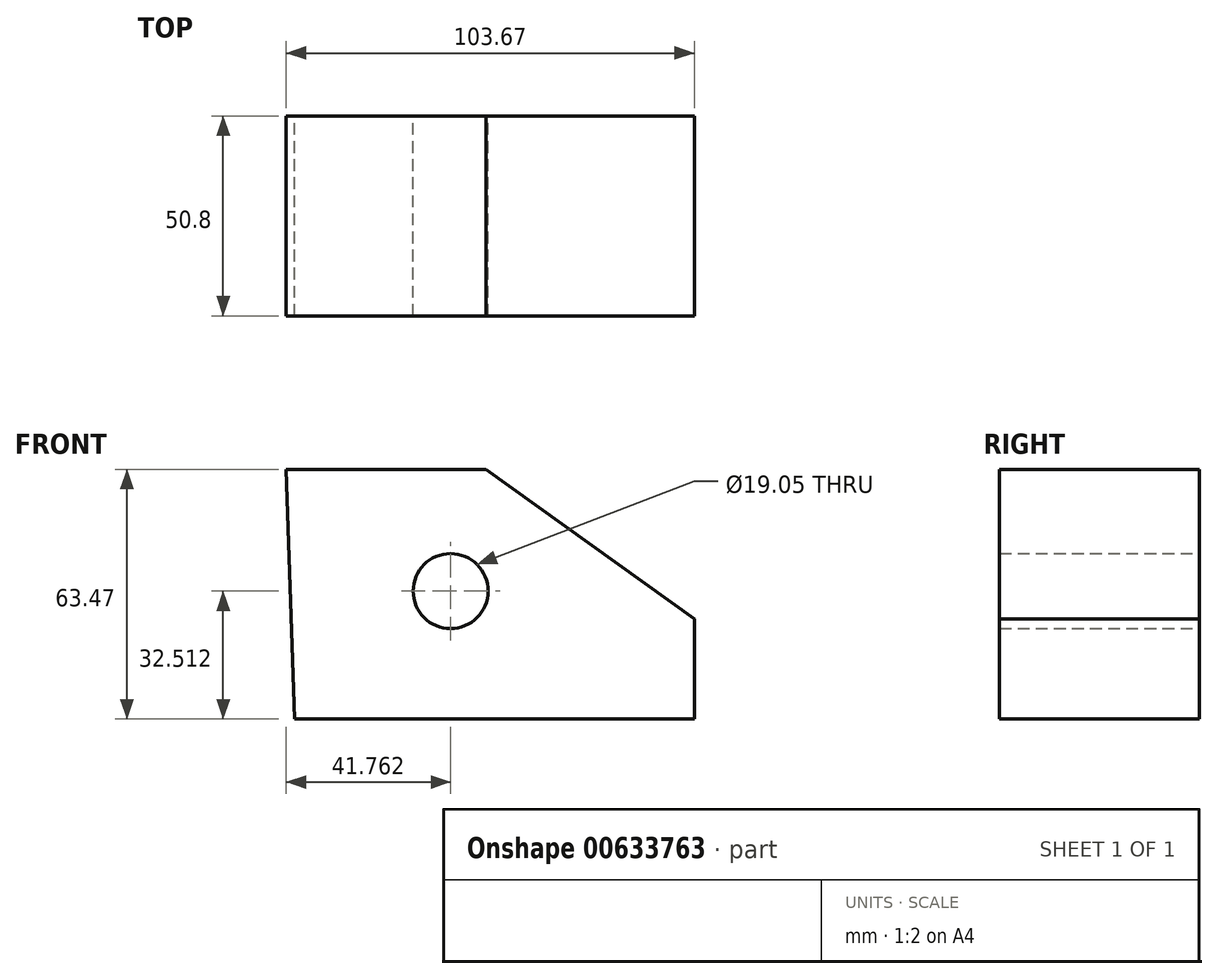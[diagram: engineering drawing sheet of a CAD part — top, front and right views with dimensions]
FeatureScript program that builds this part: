
annotation { "Feature Type Name" : "Feature", "Feature Type Description" : "" }
export const myFeature = defineFeature(function(context is Context, id is Id, definition is map)
    precondition{}
    {
        {
            var Q0;
            Q0=qCreatedBy(makeId("Front.planeOp"),FACE);
            var sketch = newSketch(context, id + "F0", { "sketchPlane" : qUnion([Q0])});
            skLineSegment(sketch, "E0", {"start": v(-48.04, 48.04) * mm, "end": v(2.76, 48.04) * mm});
            skLineSegment(sketch, "E1", {"start": v(2.76, 48.04) * mm, "end": v(55.63, 9.97) * mm});
            skLineSegment(sketch, "E2", {"start": v(55.63, 9.97) * mm, "end": v(55.63, -15.43) * mm});
            skLineSegment(sketch, "E3", {"start": v(-48.04, 48.04) * mm, "end": v(-45.97, -15.43) * mm});
            skLineSegment(sketch, "E4", {"start": v(-45.97, -15.43) * mm, "end": v(55.63, -15.43) * mm});
            skCircle(sketch, "E5", {"center": v(-6.28, 17.08) * mm, "radius": 9.53 * mm});
            skSolve(sketch);
        }
        {
            var Q0;
            Q0=makeQuery(id+"F0.imprint","IMPRINT",FACE,{"disambiguationData":[TD([[makeQuery(id+"F0.imprint","IMPRINT",EDGE,{"derivedFrom":sQuery(id+"F0.wireOp",EDGE,"E0")}),-1.0]])]});
            extrude(context, id + "F1", {"entities" : qUnion([Q0]), "depth" : 50.8 * mm, "offsetDistance" : 25.4 * mm});
        }
    });
